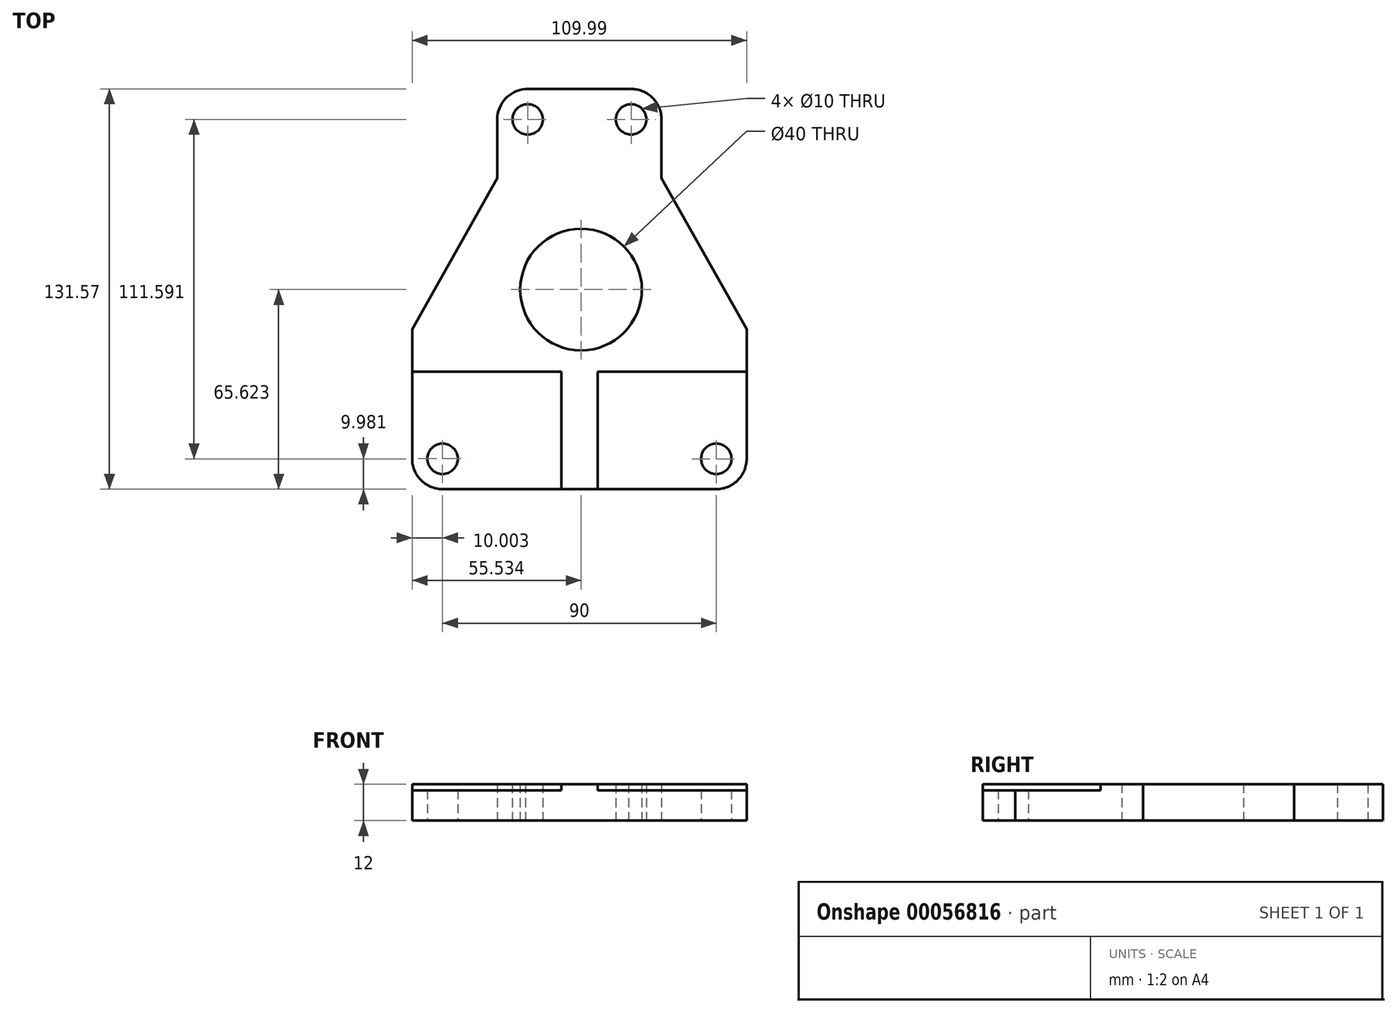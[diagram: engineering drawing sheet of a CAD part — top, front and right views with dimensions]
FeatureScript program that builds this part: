
annotation { "Feature Type Name" : "Feature", "Feature Type Description" : "" }
export const myFeature = defineFeature(function(context is Context, id is Id, definition is map)
    precondition{}
    {
        {
            var Q0;
            Q0=qCreatedBy(makeId("Top.planeOp"),FACE);
            var sketch = newSketch(context, id + "F0", { "sketchPlane" : qUnion([Q0])});
            skLineSegment(sketch, "E0", {"start": v(-52.16, -56.14) * mm, "end": v(37.84, -56.14) * mm});
            skArc(sketch, "E1", {"start": v(-62.14, -45.52) * mm, "mid": v(-59.45, -52.99) * mm, "end": v(-52.16, -56.14) * mm});
            skArc(sketch, "E2", {"start": v(37.84, -56.14) * mm, "mid": v(45.13, -52.99) * mm, "end": v(47.8, -45.52) * mm});
            skLineSegment(sketch, "E3", {"start": v(37.84, -56.14) * mm, "end": v(-1.16, -56.14) * mm});
            skLineSegment(sketch, "E4", {"start": v(-52.16, -56.14) * mm, "end": v(-13.16, -56.14) * mm});
            skCircle(sketch, "E5", {"center": v(-52.16, -46.14) * mm, "radius": 5 * mm});
            skCircle(sketch, "E6", {"center": v(37.84, -46.16) * mm, "radius": 5 * mm});
            skLineSegment(sketch, "E7", {"start": v(47.8, -45.52) * mm, "end": v(47.8, -17.52) * mm});
            skLineSegment(sketch, "E8", {"start": v(-62.14, -45.52) * mm, "end": v(-62.14, -17.52) * mm});
            skLineSegment(sketch, "E9", {"start": v(-62.14, -17.52) * mm, "end": v(47.8, -17.52) * mm});
            skLineSegment(sketch, "E10", {"start": v(-1.16, -56.14) * mm, "end": v(-1.16, -17.52) * mm});
            skLineSegment(sketch, "E11", {"start": v(-13.16, -56.14) * mm, "end": v(-13.16, -17.52) * mm});
            skLineSegment(sketch, "E12", {"start": v(47.8, -17.52) * mm, "end": v(47.8, -3.52) * mm});
            skLineSegment(sketch, "E13", {"start": v(-62.14, -17.52) * mm, "end": v(-62.14, -3.52) * mm});
            skLineSegment(sketch, "E14", {"start": v(-62.14, -3.52) * mm, "end": v(-41.14, -3.52) * mm});
            skLineSegment(sketch, "E15", {"start": v(47.8, -3.52) * mm, "end": v(26.8, -3.52) * mm});
            skArc(sketch, "E16", {"start": v(-41.14, -3.52) * mm, "mid": v(-36.42, -1.69) * mm, "end": v(-34.17, 2.85) * mm});
            skArc(sketch, "E17", {"start": v(19.83, 2.85) * mm, "mid": v(22.08, -1.69) * mm, "end": v(26.8, -3.52) * mm});
            skArc(sketch, "E18", {"start": v(19.83, 2.85) * mm, "mid": v(22.1, 14.86) * mm, "end": v(19.83, 26.86) * mm});
            skArc(sketch, "E19", {"start": v(-34.17, 26.86) * mm, "mid": v(-36.43, 14.86) * mm, "end": v(-34.17, 2.85) * mm});
            skCircle(sketch, "E20", {"center": v(-6.63, 9.48) * mm, "radius": 10 * mm});
            skCircle(sketch, "E21", {"center": v(-6.63, 9.48) * mm, "radius": 20 * mm});
            skLineSegment(sketch, "E22", {"start": v(19.83, 26.86) * mm, "end": v(19.83, 65.43) * mm});
            skLineSegment(sketch, "E23", {"start": v(-34.17, 26.86) * mm, "end": v(-34.17, 65.43) * mm});
            skArc(sketch, "E24", {"start": v(19.83, 65.43) * mm, "mid": v(16.62, 72.77) * mm, "end": v(9.05, 75.4) * mm});
            skArc(sketch, "E25", {"start": v(-24.95, 75.4) * mm, "mid": v(-31.5, 72.22) * mm, "end": v(-34.17, 65.43) * mm});
            skLineSegment(sketch, "E26", {"start": v(9.05, 75.4) * mm, "end": v(-24.95, 75.4) * mm});
            skCircle(sketch, "E27", {"center": v(9.83, 65.43) * mm, "radius": 5 * mm});
            skCircle(sketch, "E28", {"center": v(-24.17, 65.43) * mm, "radius": 5 * mm});
            skLineSegment(sketch, "E29", {"start": v(19.83, 54.43) * mm, "end": v(-34.17, 54.43) * mm});
            skLineSegment(sketch, "E30", {"start": v(47.8, -3.52) * mm, "end": v(19.83, 46.15) * mm});
            skLineSegment(sketch, "E31", {"start": v(-34.17, 46.15) * mm, "end": v(-62.14, -3.52) * mm});
            skSolve(sketch);
        }
        {
            var Q0;
            Q0=makeQuery(id+"F0.imprint","IMPRINT",FACE,{"disambiguationData":[TD([[makeQuery(id+"F0.imprint","IMPRINT",EDGE,{"derivedFrom":sQuery(id+"F0.wireOp",EDGE,"E14")}),1.0]])]});
            var Q1;
            Q1=makeQuery(id+"F0.imprint","IMPRINT",FACE,{"disambiguationData":[TD([[makeQuery(id+"F0.imprint","IMPRINT",EDGE,{"derivedFrom":sQuery(id+"F0.wireOp",EDGE,"E15")}),-1.0]])]});
            var Q2;
            Q2=makeQuery(id+"F0.imprint","IMPRINT",FACE,{"disambiguationData":[TD([[makeQuery(id+"F0.imprint","IMPRINT",EDGE,{"derivedFrom":sQuery(id+"F0.wireOp",EDGE,"E0")}),1.0]])]});
            var Q3;
            {var subQ1=sQuery(id+"F0.wireOp",EDGE,"E24");Q3=makeQuery(id+"F0.imprint","IMPRINT",FACE,{"disambiguationData":[TD([[makeQuery(id+"F0.imprint","IMPRINT",EDGE,{"derivedFrom":subQ1}),1.0]])]});}
            var Q4;
            {var subQ5=sQuery(id+"F0.wireOp",EDGE,"E12");Q4=makeQuery(id+"F0.imprint","IMPRINT",FACE,{"disambiguationData":[TD([[makeQuery(id+"F0.imprint","IMPRINT",EDGE,{"derivedFrom":subQ5}),1.0]])]});}
            extrude(context, id + "F1", {"entities" : qUnion([Q0, Q1, Q2, Q3, Q4]), "depth" : 12 * mm});
        }
        {
            var Q0;
            Q0=makeQuery(id+"F0.imprint","IMPRINT",FACE,{"disambiguationData":[TD([[makeQuery(id+"F0.imprint","IMPRINT",EDGE,{"derivedFrom":sQuery(id+"F0.wireOp",EDGE,"E1")}),1.0]])]});
            var Q1;
            Q1=makeQuery(id+"F0.imprint","IMPRINT",FACE,{"disambiguationData":[TD([[makeQuery(id+"F0.imprint","IMPRINT",EDGE,{"derivedFrom":sQuery(id+"F0.wireOp",EDGE,"E2")}),1.0]])]});
            extrude(context, id + "F2", {"entities" : qUnion([Q0, Q1]), "operationType" : NewBodyOperationType.ADD, "depth" : 10 * mm});
        }
    });
